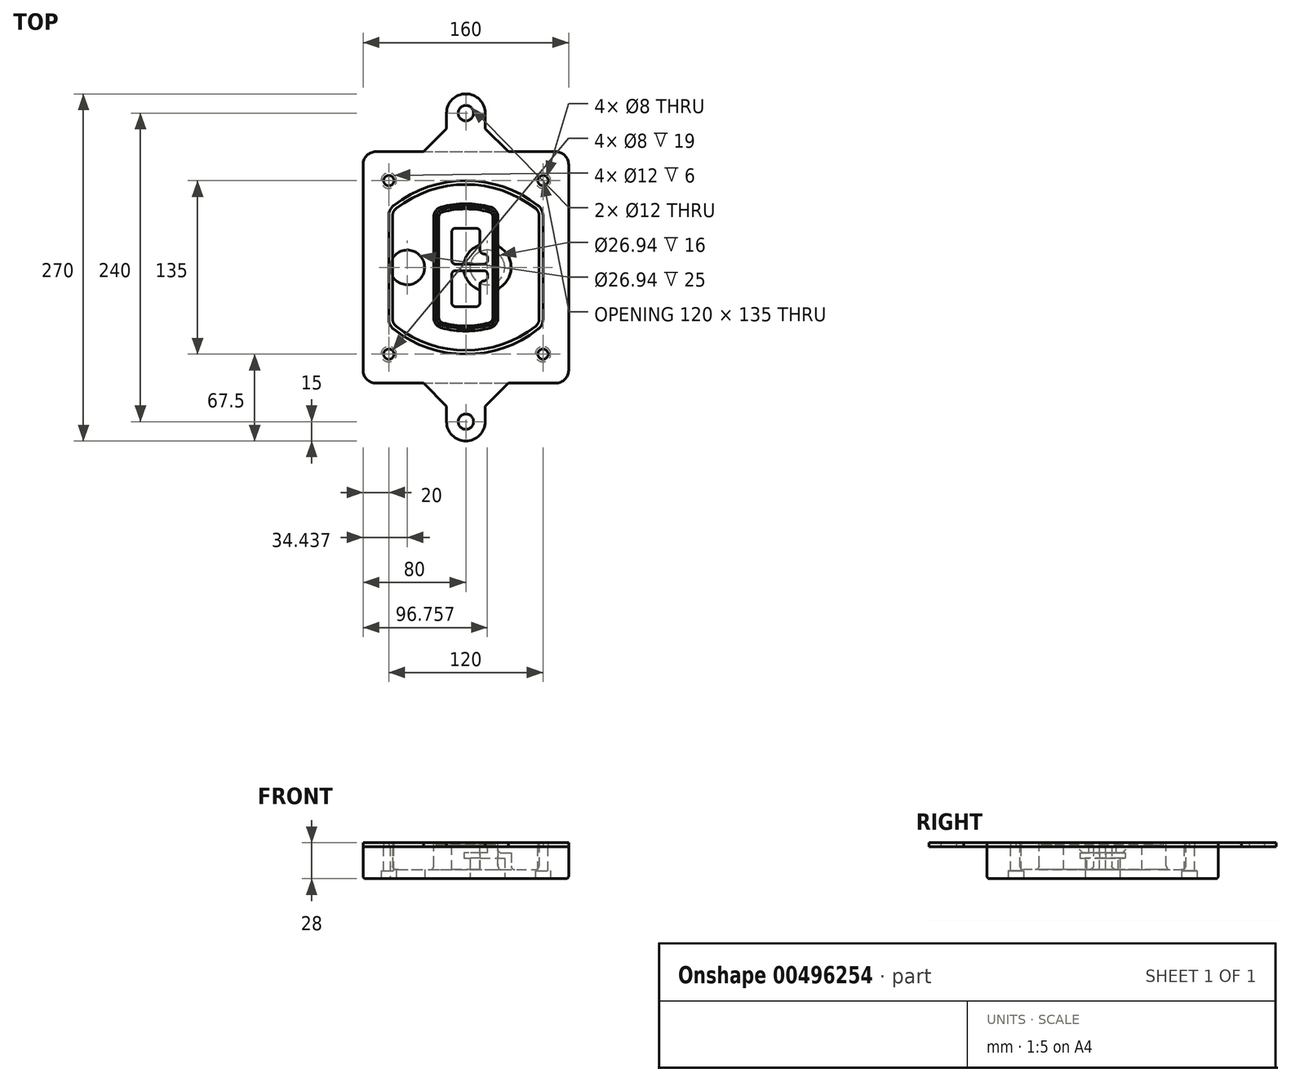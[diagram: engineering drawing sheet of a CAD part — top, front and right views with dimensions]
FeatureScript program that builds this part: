
annotation { "Feature Type Name" : "Feature", "Feature Type Description" : "" }
export const myFeature = defineFeature(function(context is Context, id is Id, definition is map)
    precondition{}
    {
        {
            var Q0;
            Q0=qCreatedBy(makeId("Top.planeOp"),FACE);
            var sketch = newSketch(context, id + "F0", { "sketchPlane" : qUnion([Q0])});
            skPoint(sketch, "E0.rect.middle", {"position": v(0, 0) * mm});
            skLineSegment(sketch, "E1.bottom", {"start": v(-70, -90) * mm, "end": v(70, -90) * mm});
            skLineSegment(sketch, "E1.top", {"start": v(-70, 90) * mm, "end": v(70, 90) * mm});
            skLineSegment(sketch, "E1.left", {"start": v(-80, -80) * mm, "end": v(-80, 80) * mm});
            skLineSegment(sketch, "E1.right", {"start": v(80, -80) * mm, "end": v(80, 80) * mm});
            skLineSegment(sketch, "E2", {"start": v(-80, 90) * mm, "end": v(80, -90) * mm, "construction": true});
            skLineSegment(sketch, "E3", {"start": v(80, 90) * mm, "end": v(-80, -90) * mm, "construction": true});
            skCircle(sketch, "E4", {"center": v(-60, 67.5) * mm, "radius": 4 * mm});
            skCircle(sketch, "E5", {"center": v(60, 67.5) * mm, "radius": 4 * mm});
            skCircle(sketch, "E6", {"center": v(60, -67.5) * mm, "radius": 4 * mm});
            skCircle(sketch, "E7", {"center": v(-60, -67.5) * mm, "radius": 4 * mm});
            skLineSegment(sketch, "E8", {"start": v(-60, 67.5) * mm, "end": v(60, 67.5) * mm, "construction": true});
            skLineSegment(sketch, "E9", {"start": v(60, 67.5) * mm, "end": v(60, -67.5) * mm, "construction": true});
            skLineSegment(sketch, "E10", {"start": v(60, -67.5) * mm, "end": v(-60, -67.5) * mm, "construction": true});
            skLineSegment(sketch, "E11", {"start": v(-60, -67.5) * mm, "end": v(-60, 67.5) * mm, "construction": true});
            skLineSegment(sketch, "E12", {"start": v(-60, 40.3) * mm, "end": v(-60, -40.3) * mm});
            skLineSegment(sketch, "E13", {"start": v(60, 40.3) * mm, "end": v(60, -40.3) * mm});
            skArc(sketch, "E14", {"start": v(56.15, 48.18) * mm, "mid": v(0, 67.5) * mm, "end": v(-56.15, 48.18) * mm});
            skArc(sketch, "E15", {"start": v(-56.15, -48.18) * mm, "mid": v(0, -67.5) * mm, "end": v(56.15, -48.18) * mm});
            skLineSegment(sketch, "E16", {"start": v(-60, 0) * mm, "end": v(60, 0) * mm, "construction": true});
            skPoint(sketch, "E17.visualSharp", {"position": v(-60, -45) * mm});
            skArc(sketch, "E17.filletArc", {"start": v(-60, -40.3) * mm, "mid": v(-58.99, -44.68) * mm, "end": v(-56.15, -48.18) * mm});
            skPoint(sketch, "E18.visualSharp", {"position": v(-60, 45) * mm});
            skArc(sketch, "E18.filletArc", {"start": v(-56.15, 48.18) * mm, "mid": v(-58.99, 44.68) * mm, "end": v(-60, 40.3) * mm});
            skPoint(sketch, "E19.visualSharp", {"position": v(60, 45) * mm});
            skArc(sketch, "E19.filletArc", {"start": v(60, 40.3) * mm, "mid": v(58.99, 44.68) * mm, "end": v(56.15, 48.18) * mm});
            skPoint(sketch, "E20.visualSharp", {"position": v(60, -45) * mm});
            skArc(sketch, "E20.filletArc", {"start": v(56.15, -48.18) * mm, "mid": v(58.99, -44.68) * mm, "end": v(60, -40.3) * mm});
            skPoint(sketch, "E21.visualSharp", {"position": v(-80, 90) * mm});
            skArc(sketch, "E21.filletArc", {"start": v(-70, 90) * mm, "mid": v(-77.07, 87.07) * mm, "end": v(-80, 80) * mm});
            skPoint(sketch, "E22.visualSharp", {"position": v(80, 90) * mm});
            skArc(sketch, "E22.filletArc", {"start": v(80, 80) * mm, "mid": v(77.07, 87.07) * mm, "end": v(70, 90) * mm});
            skPoint(sketch, "E23.visualSharp", {"position": v(80, -90) * mm});
            skArc(sketch, "E23.filletArc", {"start": v(70, -90) * mm, "mid": v(77.07, -87.07) * mm, "end": v(80, -80) * mm});
            skPoint(sketch, "E24.visualSharp", {"position": v(-80, -90) * mm});
            skArc(sketch, "E24.filletArc", {"start": v(-80, -80) * mm, "mid": v(-77.07, -87.07) * mm, "end": v(-70, -90) * mm});
            skArc(sketch, "E25.0", {"start": v(57, 40.3) * mm, "mid": v(56.3, 43.36) * mm, "end": v(54.3, 45.81) * mm});
            skLineSegment(sketch, "E25.1", {"start": v(57, 40.3) * mm, "end": v(57, -40.3) * mm});
            skArc(sketch, "E25.2", {"start": v(54.3, -45.81) * mm, "mid": v(56.3, -43.36) * mm, "end": v(57, -40.3) * mm});
            skArc(sketch, "E25.3", {"start": v(-54.3, -45.81) * mm, "mid": v(0, -64.5) * mm, "end": v(54.3, -45.81) * mm});
            skArc(sketch, "E25.4", {"start": v(-57, -40.3) * mm, "mid": v(-56.3, -43.36) * mm, "end": v(-54.3, -45.81) * mm});
            skArc(sketch, "E25.5", {"start": v(54.3, 45.81) * mm, "mid": v(0, 64.5) * mm, "end": v(-54.3, 45.81) * mm});
            skLineSegment(sketch, "E25.6", {"start": v(-57, 40.3) * mm, "end": v(-57, -40.3) * mm});
            skArc(sketch, "E25.7", {"start": v(-54.3, 45.81) * mm, "mid": v(-56.3, 43.36) * mm, "end": v(-57, 40.3) * mm});
            skArc(sketch, "E26.0", {"start": v(-58.62, 51.33) * mm, "mid": v(-62.58, 46.43) * mm, "end": v(-64, 40.3) * mm});
            skArc(sketch, "E26.1", {"start": v(58.62, 51.33) * mm, "mid": v(0, 71.5) * mm, "end": v(-58.62, 51.33) * mm});
            skArc(sketch, "E26.2", {"start": v(64, 40.3) * mm, "mid": v(62.58, 46.43) * mm, "end": v(58.62, 51.33) * mm});
            skLineSegment(sketch, "E26.3", {"start": v(64, 40.3) * mm, "end": v(64, -40.3) * mm});
            skArc(sketch, "E26.4", {"start": v(58.62, -51.33) * mm, "mid": v(62.58, -46.43) * mm, "end": v(64, -40.3) * mm});
            skLineSegment(sketch, "E26.5", {"start": v(-64, 40.3) * mm, "end": v(-64, -40.3) * mm});
            skArc(sketch, "E26.6", {"start": v(-58.62, -51.33) * mm, "mid": v(0, -71.5) * mm, "end": v(58.62, -51.33) * mm});
            skArc(sketch, "E26.7", {"start": v(-64, -40.3) * mm, "mid": v(-62.58, -46.43) * mm, "end": v(-58.62, -51.33) * mm});
            skSolve(sketch);
        }
        {
            var Q0;
            Q0=makeQuery(id+"F0.imprint","IMPRINT",FACE,{"disambiguationData":[TD([[makeQuery(id+"F0.imprint","IMPRINT",EDGE,{"derivedFrom":sQuery(id+"F0.wireOp",EDGE,"E1.bottom")}),1.0]])]});
            var Q1;
            Q1=makeQuery(id+"F0.imprint","IMPRINT",FACE,{"disambiguationData":[TD([[makeQuery(id+"F0.imprint","IMPRINT",EDGE,{"derivedFrom":sQuery(id+"F0.wireOp",EDGE,"E12")}),1.0]])]});
            var Q2;
            Q2=makeQuery(id+"F0.imprint","IMPRINT",FACE,{"disambiguationData":[TD([[makeQuery(id+"F0.imprint","IMPRINT",EDGE,{"derivedFrom":sQuery(id+"F0.wireOp",EDGE,"E25.0")}),1.0]])]});
            var Q3;
            Q3=makeQuery(id+"F0.imprint","IMPRINT",FACE,{"disambiguationData":[TD([[makeQuery(id+"F0.imprint","IMPRINT",EDGE,{"derivedFrom":sQuery(id+"F0.wireOp",EDGE,"E12")}),-1.0]])]});
            extrude(context, id + "F1", {"entities" : qUnion([Q0, Q1, Q2, Q3]), "oppositeDirection" : true, "depth" : 25 * mm});
        }
        {
            var Q0;
            Q0=makeQuery(id+"F0.imprint","IMPRINT",FACE,{"disambiguationData":[TD([[makeQuery(id+"F0.imprint","IMPRINT",EDGE,{"derivedFrom":sQuery(id+"F0.wireOp",EDGE,"E12")}),1.0]])]});
            extrude(context, id + "F2", {"entities" : qUnion([Q0]), "operationType" : NewBodyOperationType.ADD, "depth" : 3 * mm});
        }
        {
            var Q0;
            Q0=makeQuery(id+"F0.imprint","IMPRINT",FACE,{"disambiguationData":[TD([[makeQuery(id+"F0.imprint","IMPRINT",EDGE,{"derivedFrom":sQuery(id+"F0.wireOp",EDGE,"E25.0")}),1.0]])]});
            extrude(context, id + "F3", {"entities" : qUnion([Q0]), "operationType" : NewBodyOperationType.REMOVE, "oppositeDirection" : true, "depth" : 18 * mm});
        }
        {
            var Q0;
            Q0=makeQuery(id+"F2.opExtrude","CAP_FACE",FACE,{"disambiguationData":[OSD([sQuery(id+"F0.wireOp",EDGE,"E12"),sQuery(id+"F0.wireOp",EDGE,"E13"),sQuery(id+"F0.wireOp",EDGE,"E14"),sQuery(id+"F0.wireOp",EDGE,"E15"),sQuery(id+"F0.wireOp",EDGE,"E17.filletArc"),sQuery(id+"F0.wireOp",EDGE,"E18.filletArc"),sQuery(id+"F0.wireOp",EDGE,"E19.filletArc"),sQuery(id+"F0.wireOp",EDGE,"E20.filletArc"),sQuery(id+"F0.wireOp",EDGE,"E25.0"),sQuery(id+"F0.wireOp",EDGE,"E25.1"),sQuery(id+"F0.wireOp",EDGE,"E25.2"),sQuery(id+"F0.wireOp",EDGE,"E25.3"),sQuery(id+"F0.wireOp",EDGE,"E25.4"),sQuery(id+"F0.wireOp",EDGE,"E25.5"),sQuery(id+"F0.wireOp",EDGE,"E25.6"),sQuery(id+"F0.wireOp",EDGE,"E25.7")])],"isStart":false});
            var sketch = newSketch(context, id + "F4", { "sketchPlane" : qUnion([Q0])});
            skArc(sketch, "E27.0", {"start": v(-19.08, -46.97) * mm, "mid": v(0, -49.5) * mm, "end": v(19.08, -46.97) * mm});
            skArc(sketch, "E28.0", {"start": v(19.08, 46.97) * mm, "mid": v(0, 49.5) * mm, "end": v(-19.08, 46.97) * mm});
            skLineSegment(sketch, "E29", {"start": v(-25, 39.25) * mm, "end": v(-25, -39.25) * mm});
            skLineSegment(sketch, "E30", {"start": v(25, 39.25) * mm, "end": v(25, -39.25) * mm});
            skLineSegment(sketch, "E31", {"start": v(-25, 45.1) * mm, "end": v(25, 45.1) * mm, "construction": true});
            skLineSegment(sketch, "E32", {"start": v(-25, -45.1) * mm, "end": v(25, -45.1) * mm, "construction": true});
            skPoint(sketch, "E33.visualSharp", {"position": v(-25, 45.1) * mm});
            skArc(sketch, "E33.filletArc", {"start": v(-19.08, 46.97) * mm, "mid": v(-23.35, 44.11) * mm, "end": v(-25, 39.25) * mm});
            skPoint(sketch, "E34.visualSharp", {"position": v(25, 45.1) * mm});
            skArc(sketch, "E34.filletArc", {"start": v(25, 39.25) * mm, "mid": v(23.35, 44.11) * mm, "end": v(19.08, 46.97) * mm});
            skPoint(sketch, "E35.visualSharp", {"position": v(25, -45.1) * mm});
            skArc(sketch, "E35.filletArc", {"start": v(19.08, -46.97) * mm, "mid": v(23.35, -44.11) * mm, "end": v(25, -39.25) * mm});
            skPoint(sketch, "E36.visualSharp", {"position": v(-25, -45.1) * mm});
            skArc(sketch, "E36.filletArc", {"start": v(-25, -39.25) * mm, "mid": v(-23.35, -44.11) * mm, "end": v(-19.08, -46.97) * mm});
            skArc(sketch, "E37.0", {"start": v(54.3, 45.81) * mm, "mid": v(0, 64.5) * mm, "end": v(-54.3, 45.81) * mm});
            skArc(sketch, "E37.1", {"start": v(-54.3, 45.81) * mm, "mid": v(-56.3, 43.36) * mm, "end": v(-57, 40.3) * mm});
            skLineSegment(sketch, "E37.2", {"start": v(-57, 40.3) * mm, "end": v(-57, -40.3) * mm});
            skArc(sketch, "E37.3", {"start": v(-57, -40.3) * mm, "mid": v(-56.3, -43.36) * mm, "end": v(-54.3, -45.81) * mm});
            skArc(sketch, "E37.4", {"start": v(-54.3, -45.81) * mm, "mid": v(0, -64.5) * mm, "end": v(54.3, -45.81) * mm});
            skArc(sketch, "E37.5", {"start": v(54.3, -45.81) * mm, "mid": v(56.3, -43.36) * mm, "end": v(57, -40.3) * mm});
            skLineSegment(sketch, "E37.6", {"start": v(57, 40.3) * mm, "end": v(57, -40.3) * mm});
            skArc(sketch, "E37.7", {"start": v(57, 40.3) * mm, "mid": v(56.3, 43.36) * mm, "end": v(54.3, 45.81) * mm});
            skLineSegment(sketch, "E38.0", {"start": v(23, 39.25) * mm, "end": v(23, -39.25) * mm});
            skArc(sketch, "E38.1", {"start": v(18.56, -45.04) * mm, "mid": v(21.76, -42.9) * mm, "end": v(23, -39.25) * mm});
            skArc(sketch, "E38.2", {"start": v(-18.56, -45.04) * mm, "mid": v(0, -47.5) * mm, "end": v(18.56, -45.04) * mm});
            skArc(sketch, "E38.3", {"start": v(-23, -39.25) * mm, "mid": v(-21.76, -42.9) * mm, "end": v(-18.56, -45.04) * mm});
            skLineSegment(sketch, "E38.4", {"start": v(-23, 39.25) * mm, "end": v(-23, -39.25) * mm});
            skArc(sketch, "E38.5", {"start": v(23, 39.25) * mm, "mid": v(21.76, 42.9) * mm, "end": v(18.56, 45.04) * mm});
            skArc(sketch, "E38.6", {"start": v(-18.56, 45.04) * mm, "mid": v(-21.76, 42.9) * mm, "end": v(-23, 39.25) * mm});
            skArc(sketch, "E38.7", {"start": v(18.56, 45.04) * mm, "mid": v(0, 47.5) * mm, "end": v(-18.56, 45.04) * mm});
            skArc(sketch, "E39.0", {"start": v(21, 39.25) * mm, "mid": v(20.18, 41.68) * mm, "end": v(18.04, 43.1) * mm});
            skLineSegment(sketch, "E39.1", {"start": v(21, 39.25) * mm, "end": v(21, -39.25) * mm});
            skArc(sketch, "E39.2", {"start": v(18.04, -43.1) * mm, "mid": v(20.18, -41.68) * mm, "end": v(21, -39.25) * mm});
            skArc(sketch, "E39.3", {"start": v(-18.04, -43.1) * mm, "mid": v(0, -45.5) * mm, "end": v(18.04, -43.1) * mm});
            skArc(sketch, "E39.4", {"start": v(-21, -39.25) * mm, "mid": v(-20.18, -41.68) * mm, "end": v(-18.04, -43.1) * mm});
            skArc(sketch, "E39.5", {"start": v(18.04, 43.1) * mm, "mid": v(0, 45.5) * mm, "end": v(-18.04, 43.1) * mm});
            skLineSegment(sketch, "E39.6", {"start": v(-21, 39.25) * mm, "end": v(-21, -39.25) * mm});
            skArc(sketch, "E39.7", {"start": v(-18.04, 43.1) * mm, "mid": v(-20.18, 41.68) * mm, "end": v(-21, 39.25) * mm});
            skLineSegment(sketch, "E40", {"start": v(-25, 0) * mm, "end": v(25, 0) * mm, "construction": true});
            skLineSegment(sketch, "E41", {"start": v(-11, 5.5) * mm, "end": v(-11, 27.5) * mm});
            skLineSegment(sketch, "E42", {"start": v(-8, 30.5) * mm, "end": v(8, 30.5) * mm});
            skLineSegment(sketch, "E43", {"start": v(11, 27.5) * mm, "end": v(11, 13.5) * mm});
            skLineSegment(sketch, "E44", {"start": v(14, 10.5) * mm, "end": v(14, 10.5) * mm});
            skLineSegment(sketch, "E45", {"start": v(17, 7.5) * mm, "end": v(17, 5.5) * mm});
            skLineSegment(sketch, "E46", {"start": v(14, 2.5) * mm, "end": v(-8, 2.5) * mm});
            skPoint(sketch, "E47.visualSharp", {"position": v(-11, 30.5) * mm});
            skArc(sketch, "E47.filletArc", {"start": v(-8, 30.5) * mm, "mid": v(-10.12, 29.62) * mm, "end": v(-11, 27.5) * mm});
            skPoint(sketch, "E48.visualSharp", {"position": v(11, 30.5) * mm});
            skArc(sketch, "E48.filletArc", {"start": v(11, 27.5) * mm, "mid": v(10.12, 29.62) * mm, "end": v(8, 30.5) * mm});
            skPoint(sketch, "E49.visualSharp", {"position": v(11, 10.5) * mm});
            skArc(sketch, "E49.filletArc", {"start": v(11, 13.5) * mm, "mid": v(11.88, 11.38) * mm, "end": v(14, 10.5) * mm});
            skPoint(sketch, "E50.visualSharp", {"position": v(17, 10.5) * mm});
            skArc(sketch, "E50.filletArc", {"start": v(17, 7.5) * mm, "mid": v(16.12, 9.62) * mm, "end": v(14, 10.5) * mm});
            skPoint(sketch, "E51.visualSharp", {"position": v(17, 2.5) * mm});
            skArc(sketch, "E51.filletArc", {"start": v(14, 2.5) * mm, "mid": v(16.12, 3.38) * mm, "end": v(17, 5.5) * mm});
            skPoint(sketch, "E52.visualSharp", {"position": v(-11, 2.5) * mm});
            skArc(sketch, "E52.filletArc", {"start": v(-11, 5.5) * mm, "mid": v(-10.12, 3.38) * mm, "end": v(-8, 2.5) * mm});
            skLineSegment(sketch, "E53.0.MirrorCS", {"start": v(14, -2.5) * mm, "end": v(-8, -2.5) * mm});
            skArc(sketch, "E54.0.MirrorCS", {"start": v(-11, -5.5) * mm, "mid": v(-10.12, -3.38) * mm, "end": v(-8, -2.5) * mm});
            skLineSegment(sketch, "E55.0.MirrorCS", {"start": v(-11, -5.5) * mm, "end": v(-11, -27.5) * mm});
            skArc(sketch, "E56.0.MirrorCS", {"start": v(-8, -30.5) * mm, "mid": v(-10.12, -29.62) * mm, "end": v(-11, -27.5) * mm});
            skLineSegment(sketch, "E57.0.MirrorCS", {"start": v(-8, -30.5) * mm, "end": v(8, -30.5) * mm});
            skArc(sketch, "E58.0.MirrorCS", {"start": v(11, -27.5) * mm, "mid": v(10.12, -29.62) * mm, "end": v(8, -30.5) * mm});
            skLineSegment(sketch, "E59.0.MirrorCS", {"start": v(11, -27.5) * mm, "end": v(11, -13.5) * mm});
            skArc(sketch, "E60.0.MirrorCS", {"start": v(11, -13.5) * mm, "mid": v(11.88, -11.38) * mm, "end": v(14, -10.5) * mm});
            skArc(sketch, "E61.0.MirrorCS", {"start": v(17, -7.5) * mm, "mid": v(16.12, -9.62) * mm, "end": v(14, -10.5) * mm});
            skLineSegment(sketch, "E62.0.MirrorCS", {"start": v(17, -7.5) * mm, "end": v(17, -5.5) * mm});
            skArc(sketch, "E63.0.MirrorCS", {"start": v(14, -2.5) * mm, "mid": v(16.12, -3.38) * mm, "end": v(17, -5.5) * mm});
            skSolve(sketch);
        }
        {
            var Q0;
            Q0=makeQuery(id+"F4.imprint","IMPRINT",FACE,{"disambiguationData":[TD([[makeQuery(id+"F4.imprint","IMPRINT",EDGE,{"derivedFrom":sQuery(id+"F4.wireOp",EDGE,"E27.0")}),1.0]])]});
            var Q1;
            Q1=makeQuery(id+"F4.imprint","IMPRINT",FACE,{"disambiguationData":[TD([[makeQuery(id+"F4.imprint","IMPRINT",EDGE,{"derivedFrom":sQuery(id+"F4.wireOp",EDGE,"E38.0")}),-1.0]])]});
            var Q2;
            Q2=makeQuery(id+"F4.imprint","IMPRINT",FACE,{"disambiguationData":[TD([[makeQuery(id+"F4.imprint","IMPRINT",EDGE,{"derivedFrom":sQuery(id+"F4.wireOp",EDGE,"E39.0")}),1.0]])]});
            extrude(context, id + "F5", {"entities" : qUnion([Q0, Q1, Q2]), "operationType" : NewBodyOperationType.ADD, "endBound" : BoundingType.UP_TO_NEXT, "oppositeDirection" : true, "depth" : 25 * mm});
        }
        {
            var Q0;
            Q0=makeQuery(id+"F4.imprint","IMPRINT",FACE,{"disambiguationData":[TD([[makeQuery(id+"F4.imprint","IMPRINT",EDGE,{"derivedFrom":sQuery(id+"F4.wireOp",EDGE,"E38.0")}),-1.0]])]});
            extrude(context, id + "F6", {"entities" : qUnion([Q0]), "operationType" : NewBodyOperationType.REMOVE, "oppositeDirection" : true, "depth" : 2 * mm});
        }
        {
            var Q0;
            Q0=makeQuery(id+"F1.opExtrude","CAP_FACE",FACE,{"disambiguationData":[OSD([sQuery(id+"F0.wireOp",EDGE,"E1.bottom"),sQuery(id+"F0.wireOp",EDGE,"E1.top"),sQuery(id+"F0.wireOp",EDGE,"E1.left"),sQuery(id+"F0.wireOp",EDGE,"E1.right"),sQuery(id+"F0.wireOp",EDGE,"E4"),sQuery(id+"F0.wireOp",EDGE,"E5"),sQuery(id+"F0.wireOp",EDGE,"E6"),sQuery(id+"F0.wireOp",EDGE,"E7"),sQuery(id+"F0.wireOp",EDGE,"E21.filletArc"),sQuery(id+"F0.wireOp",EDGE,"E22.filletArc"),sQuery(id+"F0.wireOp",EDGE,"E23.filletArc"),sQuery(id+"F0.wireOp",EDGE,"E24.filletArc")])],"isStart":false});
            var sketch = newSketch(context, id + "F7", { "sketchPlane" : qUnion([Q0])});
            skCircle(sketch, "E64", {"center": v(16.76, 0) * mm, "radius": 13.47 * mm});
            skCircle(sketch, "E65", {"center": v(-45.56, 0) * mm, "radius": 13.47 * mm});
            skLineSegment(sketch, "E66", {"start": v(80, 0) * mm, "end": v(-80, 0) * mm});
            skCircle(sketch, "E67", {"center": v(16.76, 0) * mm, "radius": 18.47 * mm});
            skCircle(sketch, "E68", {"center": v(60, -67.5) * mm, "radius": 6 * mm});
            skCircle(sketch, "E69", {"center": v(-60, -67.5) * mm, "radius": 6 * mm});
            skCircle(sketch, "E70", {"center": v(-60, 67.5) * mm, "radius": 6 * mm});
            skCircle(sketch, "E71", {"center": v(60, 67.5) * mm, "radius": 6 * mm});
            skSolve(sketch);
        }
        {
            var Q0;
            {var subQ1=sQuery(id+"F7.wireOp",EDGE,"E66");var subQ4=sQuery(id+"F7.wireOp",EDGE,"E64");var subQ6=makeQuery(id+"F7.imprint","INTERSECT",VERTEX,{"disambiguationData":[OD(0.0)],"derivedFrom":[subQ4,subQ1]});Q0=makeQuery(id+"F7.imprint","IMPRINT",FACE,{"disambiguationData":[TD([[makeQuery(id+"F7.imprint","IMPRINT",EDGE,{"disambiguationData":[TD([[subQ6,-1.0]])],"derivedFrom":subQ4}),-1.0]])]});}
            var Q1;
            {var subQ0=sQuery(id+"F7.wireOp",EDGE,"E66");var subQ1=sQuery(id+"F7.wireOp",EDGE,"E64");var subQ3=makeQuery(id+"F7.imprint","INTERSECT",VERTEX,{"disambiguationData":[OD(0.0)],"derivedFrom":[subQ1,subQ0]});Q1=makeQuery(id+"F7.imprint","IMPRINT",FACE,{"disambiguationData":[TD([[makeQuery(id+"F7.imprint","IMPRINT",EDGE,{"disambiguationData":[TD([[subQ3,-1.0]])],"derivedFrom":subQ1}),1.0]])]});}
            var Q2;
            {var subQ0=sQuery(id+"F7.wireOp",EDGE,"E66");var subQ1=sQuery(id+"F7.wireOp",EDGE,"E64");var subQ3=makeQuery(id+"F7.imprint","INTERSECT",VERTEX,{"disambiguationData":[OD(0.0)],"derivedFrom":[subQ1,subQ0]});Q2=makeQuery(id+"F7.imprint","IMPRINT",FACE,{"disambiguationData":[TD([[makeQuery(id+"F7.imprint","IMPRINT",EDGE,{"disambiguationData":[TD([[subQ3,1.0]])],"derivedFrom":subQ1}),1.0]])]});}
            var Q3;
            {var subQ1=sQuery(id+"F7.wireOp",EDGE,"E66");var subQ4=sQuery(id+"F7.wireOp",EDGE,"E64");var subQ6=makeQuery(id+"F7.imprint","INTERSECT",VERTEX,{"disambiguationData":[OD(0.0)],"derivedFrom":[subQ4,subQ1]});Q3=makeQuery(id+"F7.imprint","IMPRINT",FACE,{"disambiguationData":[TD([[makeQuery(id+"F7.imprint","IMPRINT",EDGE,{"disambiguationData":[TD([[subQ6,1.0]])],"derivedFrom":subQ4}),-1.0]])]});}
            extrude(context, id + "F8", {"entities" : qUnion([Q0, Q1, Q2, Q3]), "operationType" : NewBodyOperationType.ADD, "oppositeDirection" : true, "depth" : 20 * mm});
        }
        {
            var Q0;
            {var subQ0=sQuery(id+"F7.wireOp",EDGE,"E66");var subQ1=sQuery(id+"F7.wireOp",EDGE,"E64");var subQ3=makeQuery(id+"F7.imprint","INTERSECT",VERTEX,{"disambiguationData":[OD(0.0)],"derivedFrom":[subQ1,subQ0]});Q0=makeQuery(id+"F7.imprint","IMPRINT",FACE,{"disambiguationData":[TD([[makeQuery(id+"F7.imprint","IMPRINT",EDGE,{"disambiguationData":[TD([[subQ3,-1.0]])],"derivedFrom":subQ1}),1.0]])]});}
            var Q1;
            {var subQ0=sQuery(id+"F7.wireOp",EDGE,"E66");var subQ1=sQuery(id+"F7.wireOp",EDGE,"E64");var subQ3=makeQuery(id+"F7.imprint","INTERSECT",VERTEX,{"disambiguationData":[OD(0.0)],"derivedFrom":[subQ1,subQ0]});Q1=makeQuery(id+"F7.imprint","IMPRINT",FACE,{"disambiguationData":[TD([[makeQuery(id+"F7.imprint","IMPRINT",EDGE,{"disambiguationData":[TD([[subQ3,1.0]])],"derivedFrom":subQ1}),1.0]])]});}
            extrude(context, id + "F9", {"entities" : qUnion([Q0, Q1]), "operationType" : NewBodyOperationType.REMOVE, "oppositeDirection" : true, "depth" : 16 * mm});
        }
        {
            var Q0;
            {var subQ0=sQuery(id+"F7.wireOp",EDGE,"E66");var subQ1=sQuery(id+"F7.wireOp",EDGE,"E65");var subQ3=makeQuery(id+"F7.imprint","INTERSECT",VERTEX,{"disambiguationData":[OD(0.0)],"derivedFrom":[subQ1,subQ0]});Q0=makeQuery(id+"F7.imprint","IMPRINT",FACE,{"disambiguationData":[TD([[makeQuery(id+"F7.imprint","IMPRINT",EDGE,{"disambiguationData":[TD([[subQ3,-1.0]])],"derivedFrom":subQ1}),1.0]])]});}
            var Q1;
            {var subQ0=sQuery(id+"F7.wireOp",EDGE,"E66");var subQ1=sQuery(id+"F7.wireOp",EDGE,"E65");var subQ3=makeQuery(id+"F7.imprint","INTERSECT",VERTEX,{"disambiguationData":[OD(0.0)],"derivedFrom":[subQ1,subQ0]});Q1=makeQuery(id+"F7.imprint","IMPRINT",FACE,{"disambiguationData":[TD([[makeQuery(id+"F7.imprint","IMPRINT",EDGE,{"disambiguationData":[TD([[subQ3,1.0]])],"derivedFrom":subQ1}),1.0]])]});}
            extrude(context, id + "F10", {"entities" : qUnion([Q0, Q1]), "operationType" : NewBodyOperationType.REMOVE, "oppositeDirection" : true, "depth" : 25 * mm});
        }
        {
            var Q0;
            Q0=makeQuery(id+"F7.imprint","IMPRINT",FACE,{"disambiguationData":[TD([[makeQuery(id+"F7.imprint","IMPRINT",EDGE,{"derivedFrom":sQuery(id+"F7.wireOp",EDGE,"E68")}),1.0]])]});
            var Q1;
            Q1=makeQuery(id+"F7.imprint","IMPRINT",FACE,{"disambiguationData":[TD([[makeQuery(id+"F7.imprint","IMPRINT",EDGE,{"derivedFrom":makeQuery(id+"F1.opExtrude","CAP_EDGE",EDGE,{"disambiguationData":[OSD([sQuery(id+"F0.wireOp",EDGE,"E5")])],"isStart":false})}),-1.0]])]});
            var Q2;
            Q2=makeQuery(id+"F7.imprint","IMPRINT",FACE,{"disambiguationData":[TD([[makeQuery(id+"F7.imprint","IMPRINT",EDGE,{"derivedFrom":sQuery(id+"F7.wireOp",EDGE,"E69")}),1.0]])]});
            var Q3;
            Q3=makeQuery(id+"F7.imprint","IMPRINT",FACE,{"disambiguationData":[TD([[makeQuery(id+"F7.imprint","IMPRINT",EDGE,{"derivedFrom":makeQuery(id+"F1.opExtrude","CAP_EDGE",EDGE,{"disambiguationData":[OSD([sQuery(id+"F0.wireOp",EDGE,"E4")])],"isStart":false})}),-1.0]])]});
            var Q4;
            Q4=makeQuery(id+"F7.imprint","IMPRINT",FACE,{"disambiguationData":[TD([[makeQuery(id+"F7.imprint","IMPRINT",EDGE,{"derivedFrom":sQuery(id+"F7.wireOp",EDGE,"E70")}),1.0]])]});
            var Q5;
            Q5=makeQuery(id+"F7.imprint","IMPRINT",FACE,{"disambiguationData":[TD([[makeQuery(id+"F7.imprint","IMPRINT",EDGE,{"derivedFrom":makeQuery(id+"F1.opExtrude","CAP_EDGE",EDGE,{"disambiguationData":[OSD([sQuery(id+"F0.wireOp",EDGE,"E7")])],"isStart":false})}),-1.0]])]});
            var Q6;
            Q6=makeQuery(id+"F7.imprint","IMPRINT",FACE,{"disambiguationData":[TD([[makeQuery(id+"F7.imprint","IMPRINT",EDGE,{"derivedFrom":sQuery(id+"F7.wireOp",EDGE,"E71")}),1.0]])]});
            var Q7;
            Q7=makeQuery(id+"F7.imprint","IMPRINT",FACE,{"disambiguationData":[TD([[makeQuery(id+"F7.imprint","IMPRINT",EDGE,{"derivedFrom":makeQuery(id+"F1.opExtrude","CAP_EDGE",EDGE,{"disambiguationData":[OSD([sQuery(id+"F0.wireOp",EDGE,"E6")])],"isStart":false})}),-1.0]])]});
            extrude(context, id + "F11", {"entities" : qUnion([Q0, Q1, Q2, Q3, Q4, Q5, Q6, Q7]), "operationType" : NewBodyOperationType.REMOVE, "oppositeDirection" : true, "depth" : 6 * mm});
        }
        {
            var Q0;
            Q0=makeQuery(id+"F9.boolean.opBoolean","COPY",FACE,{"derivedFrom":makeQuery(id+"F9.opExtrude","CAP_FACE",FACE,{"disambiguationData":[OSD([sQuery(id+"F7.wireOp",EDGE,"E64")])],"isStart":false})});
            var sketch = newSketch(context, id + "F12", { "sketchPlane" : qUnion([Q0])});
            skArc(sketch, "E72.0", {"start": v(11, 17.55) * mm, "mid": v(2.57, 11.82) * mm, "end": v(-1.54, 2.5) * mm});
            skArc(sketch, "E72.1", {"start": v(-1.54, -2.5) * mm, "mid": v(2.57, -11.82) * mm, "end": v(11, -17.55) * mm});
            skLineSegment(sketch, "E73", {"start": v(-1.54, -2.5) * mm, "end": v(14, -2.5) * mm});
            skLineSegment(sketch, "E74.0", {"start": v(14, 2.5) * mm, "end": v(-1.54, 2.5) * mm});
            skArc(sketch, "E74.1", {"start": v(14, 2.5) * mm, "mid": v(16.12, 3.38) * mm, "end": v(17, 5.5) * mm});
            skLineSegment(sketch, "E74.2", {"start": v(17, 7.5) * mm, "end": v(17, 5.5) * mm});
            skArc(sketch, "E74.3", {"start": v(17, 7.5) * mm, "mid": v(16.12, 9.62) * mm, "end": v(14, 10.5) * mm});
            skArc(sketch, "E74.4", {"start": v(11, 13.5) * mm, "mid": v(11.88, 11.38) * mm, "end": v(14, 10.5) * mm});
            skLineSegment(sketch, "E74.5", {"start": v(11, 17.55) * mm, "end": v(11, 13.5) * mm});
            skLineSegment(sketch, "E74.7", {"start": v(14, -2.5) * mm, "end": v(-1.54, -2.5) * mm});
            skArc(sketch, "E74.8", {"start": v(14, -2.5) * mm, "mid": v(16.12, -3.38) * mm, "end": v(17, -5.5) * mm});
            skLineSegment(sketch, "E74.9", {"start": v(17, -7.5) * mm, "end": v(17, -5.5) * mm});
            skArc(sketch, "E74.10", {"start": v(17, -7.5) * mm, "mid": v(16.12, -9.62) * mm, "end": v(14, -10.5) * mm});
            skArc(sketch, "E74.11", {"start": v(11, -13.5) * mm, "mid": v(11.88, -11.38) * mm, "end": v(14, -10.5) * mm});
            skLineSegment(sketch, "E74.12", {"start": v(11, -17.55) * mm, "end": v(11, -13.5) * mm});
            skPoint(sketch, "E75.orphan", {"position": v(11, -27.5) * mm});
            skPoint(sketch, "E76.orphan", {"position": v(-8, -2.5) * mm});
            skPoint(sketch, "E77.orphan", {"position": v(-8, 2.5) * mm});
            skPoint(sketch, "E78.orphan", {"position": v(11, 27.5) * mm});
            skSolve(sketch);
        }
        {
            var Q0;
            {var subQ7=sQuery(id+"F12.wireOp",EDGE,"E72.0");var subQ14=sQuery(id+"F12.wireOp",EDGE,"E72.1");var subQ16=sQuery(id+"F12.wireOp",EDGE,"E74.1");var subQ18=sQuery(id+"F12.wireOp",EDGE,"E74.8");Q0=qUnion([makeQuery(id+"F12.imprint","IMPRINT",FACE,{"disambiguationData":[TD([[makeQuery(id+"F12.imprint","IMPRINT",EDGE,{"derivedFrom":subQ7}),1.0]])]}),makeQuery(id+"F12.imprint","IMPRINT",FACE,{"disambiguationData":[TD([[makeQuery(id+"F12.imprint","IMPRINT",EDGE,{"derivedFrom":subQ14}),1.0]])]}),makeQuery(id+"F12.imprint","IMPRINT",FACE,{"disambiguationData":[TD([[makeQuery(id+"F12.imprint","IMPRINT",EDGE,{"derivedFrom":subQ16}),1.0]])]}),makeQuery(id+"F12.imprint","IMPRINT",FACE,{"disambiguationData":[TD([[makeQuery(id+"F12.imprint","IMPRINT",EDGE,{"derivedFrom":subQ18}),-1.0]])]})]);}
            var Q1;
            Q1 = qSketchRegion(id + "F17", true);
            var Q2;
            Q2=makeQuery(id+"F5.boolean.opBoolean","SPLIT",FACE,{"disambiguationData":[TD([makeQuery(id+"F5.opExtrude","SWEPT_FACE",FACE,{"disambiguationData":[OSD([sQuery(id+"F4.wireOp",EDGE,"E41")])]})])],"derivedFrom":makeQuery(id+"F3.boolean.opBoolean","COPY",FACE,{"derivedFrom":makeQuery(id+"F3.opExtrude","CAP_FACE",FACE,{"disambiguationData":[OSD([sQuery(id+"F0.wireOp",EDGE,"E25.0"),sQuery(id+"F0.wireOp",EDGE,"E25.1"),sQuery(id+"F0.wireOp",EDGE,"E25.2"),sQuery(id+"F0.wireOp",EDGE,"E25.3"),sQuery(id+"F0.wireOp",EDGE,"E25.4"),sQuery(id+"F0.wireOp",EDGE,"E25.5"),sQuery(id+"F0.wireOp",EDGE,"E25.6"),sQuery(id+"F0.wireOp",EDGE,"E25.7")])],"isStart":false})})});
            extrude(context, id + "F13", {"entities" : qUnion([Q0, Q1]), "operationType" : NewBodyOperationType.REMOVE, "endBound" : BoundingType.UP_TO_SURFACE, "endBoundEntityFace" : qUnion([Q2]), "depth" : 25 * mm});
        }
        {
            var Q0;
            Q0=makeQuery(id+"F3.boolean.opBoolean","COPY",EDGE,{"derivedFrom":makeQuery(id+"F3.opExtrude","CAP_EDGE",EDGE,{"disambiguationData":[OSD([sQuery(id+"F0.wireOp",EDGE,"E25.6")])],"isStart":false})});
            var Q1;
            Q1=makeQuery(id+"F8.boolean.opBoolean","INTERSECT",EDGE,{"derivedFrom":[makeQuery(id+"F5.opExtrude","SWEPT_FACE",FACE,{"disambiguationData":[OSD([sQuery(id+"F4.wireOp",EDGE,"E30")])]}),makeQuery(id+"F8.opExtrude","CAP_FACE",FACE,{"disambiguationData":[OSD([sQuery(id+"F7.wireOp",EDGE,"E67")])],"isStart":false})]});
            var Q2;
            Q2=makeQuery(id+"F8.boolean.opBoolean","INTERSECT",EDGE,{"disambiguationData":[OD(1.0)],"derivedFrom":[makeQuery(id+"F5.opExtrude","SWEPT_FACE",FACE,{"disambiguationData":[OSD([sQuery(id+"F4.wireOp",EDGE,"E30")])]}),makeQuery(id+"F8.opExtrude","SWEPT_FACE",FACE,{"disambiguationData":[OSD([sQuery(id+"F7.wireOp",EDGE,"E67")])]})]});
            var Q3;
            {var subQ0=sQuery(id+"F4.wireOp",EDGE,"E30");Q3=makeQuery(id+"F8.boolean.opBoolean","SPLIT",EDGE,{"disambiguationData":[TD([makeQuery(id+"F5.opExtrude","SWEPT_FACE",FACE,{"disambiguationData":[OSD([sQuery(id+"F4.wireOp",EDGE,"E35.filletArc")])]})])],"derivedFrom":makeQuery(id+"F5.opExtrude","CAP_EDGE",EDGE,{"disambiguationData":[OSD([subQ0])],"isStart":false})});}
            var Q4;
            {var subQ0=sQuery(id+"F0.wireOp",EDGE,"E25.7");var subQ1=sQuery(id+"F0.wireOp",EDGE,"E25.1");var subQ2=sQuery(id+"F0.wireOp",EDGE,"E25.6");var subQ3=sQuery(id+"F0.wireOp",EDGE,"E25.5");var subQ4=sQuery(id+"F0.wireOp",EDGE,"E25.4");var subQ5=sQuery(id+"F0.wireOp",EDGE,"E25.0");var subQ6=sQuery(id+"F0.wireOp",EDGE,"E25.2");var subQ7=sQuery(id+"F0.wireOp",EDGE,"E25.3");Q4=makeQuery(id+"F8.boolean.opBoolean","INTERSECT",EDGE,{"derivedFrom":[makeQuery(id+"F5.boolean.opBoolean","SPLIT",FACE,{"disambiguationData":[TD([makeQuery(id+"F2.opExtrude","SWEPT_FACE",FACE,{"disambiguationData":[OSD([subQ5])]})])],"derivedFrom":makeQuery(id+"F3.boolean.opBoolean","COPY",FACE,{"derivedFrom":makeQuery(id+"F3.opExtrude","CAP_FACE",FACE,{"disambiguationData":[OSD([subQ5,subQ1,subQ6,subQ7,subQ4,subQ3,subQ2,subQ0])],"isStart":false})})}),makeQuery(id+"F8.opExtrude","SWEPT_FACE",FACE,{"disambiguationData":[OSD([sQuery(id+"F7.wireOp",EDGE,"E67")])]})]});}
            var Q5;
            Q5=makeQuery(id+"F8.boolean.opBoolean","INTERSECT",EDGE,{"disambiguationData":[OD(0.0)],"derivedFrom":[makeQuery(id+"F5.opExtrude","SWEPT_FACE",FACE,{"disambiguationData":[OSD([sQuery(id+"F4.wireOp",EDGE,"E30")])]}),makeQuery(id+"F8.opExtrude","SWEPT_FACE",FACE,{"disambiguationData":[OSD([sQuery(id+"F7.wireOp",EDGE,"E67")])]})]});
            fillet(context, id + "F14", {"entities" : qUnion([Q0, Q1, Q2, Q3, Q4, Q5]), "radius" : 3 * mm, "tangentPropagation" : true, "allowEdgeOverflow" : false});
        }
        {
            var Q0;
            Q0=makeQuery(id+"F1.opExtrude","CAP_EDGE",EDGE,{"disambiguationData":[OSD([sQuery(id+"F0.wireOp",EDGE,"E1.bottom")])],"isStart":false});
            fillet(context, id + "F15", {"entities" : qUnion([Q0]), "radius" : 2 * mm, "tangentPropagation" : true, "allowEdgeOverflow" : false});
        }
        {
            var Q0;
            {var subQ0=sQuery(id+"F0.wireOp",EDGE,"E21.filletArc");var subQ1=sQuery(id+"F0.wireOp",EDGE,"E7");var subQ2=sQuery(id+"F0.wireOp",EDGE,"E6");var subQ3=sQuery(id+"F0.wireOp",EDGE,"E5");var subQ4=sQuery(id+"F0.wireOp",EDGE,"E4");var subQ5=sQuery(id+"F0.wireOp",EDGE,"E22.filletArc");var subQ6=sQuery(id+"F0.wireOp",EDGE,"E1.bottom");var subQ7=sQuery(id+"F0.wireOp",EDGE,"E1.right");var subQ8=sQuery(id+"F0.wireOp",EDGE,"E1.top");var subQ9=sQuery(id+"F0.wireOp",EDGE,"E1.left");var subQ10=sQuery(id+"F0.wireOp",EDGE,"E23.filletArc");var subQ11=sQuery(id+"F0.wireOp",EDGE,"E24.filletArc");Q0=makeQuery(id+"F2.boolean.opBoolean","SPLIT",FACE,{"disambiguationData":[TD([makeQuery(id+"F1.opExtrude","SWEPT_FACE",FACE,{"disambiguationData":[OSD([subQ6])]})])],"derivedFrom":makeQuery(id+"F1.opExtrude","CAP_FACE",FACE,{"disambiguationData":[OSD([subQ6,subQ8,subQ9,subQ7,subQ4,subQ3,subQ2,subQ1,subQ0,subQ5,subQ10,subQ11])],"isStart":true})});}
            var sketch = newSketch(context, id + "F16", { "sketchPlane" : qUnion([Q0])});
            skLineSegment(sketch, "E79", {"start": v(0, 90) * mm, "end": v(0, 120) * mm, "construction": true});
            skCircle(sketch, "E80", {"center": v(0, 120) * mm, "radius": 6 * mm});
            skLineSegment(sketch, "E81", {"start": v(-33, 90) * mm, "end": v(-15, 108) * mm});
            skLineSegment(sketch, "E82", {"start": v(-15, 108) * mm, "end": v(-15, 120) * mm});
            skLineSegment(sketch, "E83", {"start": v(33, 90) * mm, "end": v(15, 108) * mm});
            skLineSegment(sketch, "E84", {"start": v(15, 108) * mm, "end": v(15, 120) * mm});
            skArc(sketch, "E85", {"start": v(15, 120) * mm, "mid": v(0, 135) * mm, "end": v(-15, 120) * mm});
            skLineSegment(sketch, "E86", {"start": v(-80, 0) * mm, "end": v(80, 0) * mm, "construction": true});
            skLineSegment(sketch, "E87.MirrorCS", {"start": v(33, -90) * mm, "end": v(15, -108) * mm});
            skLineSegment(sketch, "E88.MirrorCS", {"start": v(15, -108) * mm, "end": v(15, -120) * mm});
            skArc(sketch, "E89.MirrorCS", {"start": v(15, -120) * mm, "mid": v(0, -135) * mm, "end": v(-15, -120) * mm});
            skLineSegment(sketch, "E90.MirrorCS", {"start": v(-15, -108) * mm, "end": v(-15, -120) * mm});
            skLineSegment(sketch, "E91.MirrorCS", {"start": v(-33, -90) * mm, "end": v(-15, -108) * mm});
            skCircle(sketch, "E92.MirrorC", {"center": v(0, -120) * mm, "radius": 6 * mm});
            skLineSegment(sketch, "E93.MirrorCS", {"start": v(0, -90) * mm, "end": v(0, -120) * mm, "construction": true});
            skSolve(sketch);
        }
        {
            var Q0;
            Q0=makeQuery(id+"F16.imprint","IMPRINT",FACE,{"disambiguationData":[TD([[makeQuery(id+"F16.imprint","IMPRINT",EDGE,{"derivedFrom":makeQuery(id+"F1.opExtrude","CAP_EDGE",EDGE,{"disambiguationData":[OSD([sQuery(id+"F0.wireOp",EDGE,"E1.bottom")])],"isStart":true})}),1.0]])]});
            var sketch = newSketch(context, id + "F17", { "sketchPlane" : qUnion([Q0])});
            skSolve(sketch);
        }
        {
            var Q0;
            {var subQ0=sQuery(id+"F16.wireOp",EDGE,"E87.MirrorCS");Q0=makeQuery(id+"F16.imprint","IMPRINT",FACE,{"disambiguationData":[TD([[makeQuery(id+"F16.imprint","IMPRINT",EDGE,{"derivedFrom":subQ0}),-1.0]])]});}
            var Q1;
            Q1=makeQuery(id+"F16.imprint","IMPRINT",FACE,{"disambiguationData":[TD([[makeQuery(id+"F16.imprint","IMPRINT",EDGE,{"derivedFrom":sQuery(id+"F16.wireOp",EDGE,"E80")}),-1.0]])]});
            var Q2;
            Q2=makeQuery(id+"F16.imprint","IMPRINT",FACE,{"disambiguationData":[TD([[makeQuery(id+"F16.imprint","IMPRINT",EDGE,{"derivedFrom":makeQuery(id+"F1.opExtrude","CAP_EDGE",EDGE,{"disambiguationData":[OSD([sQuery(id+"F0.wireOp",EDGE,"E1.left")])],"isStart":true})}),-1.0]])]});
            var Q3;
            Q3=makeQuery(id+"F2.opExtrude","CAP_FACE",FACE,{"disambiguationData":[OSD([sQuery(id+"F0.wireOp",EDGE,"E12"),sQuery(id+"F0.wireOp",EDGE,"E13"),sQuery(id+"F0.wireOp",EDGE,"E14"),sQuery(id+"F0.wireOp",EDGE,"E15"),sQuery(id+"F0.wireOp",EDGE,"E17.filletArc"),sQuery(id+"F0.wireOp",EDGE,"E18.filletArc"),sQuery(id+"F0.wireOp",EDGE,"E19.filletArc"),sQuery(id+"F0.wireOp",EDGE,"E20.filletArc"),sQuery(id+"F0.wireOp",EDGE,"E25.0"),sQuery(id+"F0.wireOp",EDGE,"E25.1"),sQuery(id+"F0.wireOp",EDGE,"E25.2"),sQuery(id+"F0.wireOp",EDGE,"E25.3"),sQuery(id+"F0.wireOp",EDGE,"E25.4"),sQuery(id+"F0.wireOp",EDGE,"E25.5"),sQuery(id+"F0.wireOp",EDGE,"E25.6"),sQuery(id+"F0.wireOp",EDGE,"E25.7")])],"isStart":false});
            extrude(context, id + "F18", {"entities" : qUnion([Q0, Q1, Q2]), "endBound" : BoundingType.UP_TO_SURFACE, "endBoundEntityFace" : qUnion([Q3]), "depth" : 25 * mm});
        }
    });
